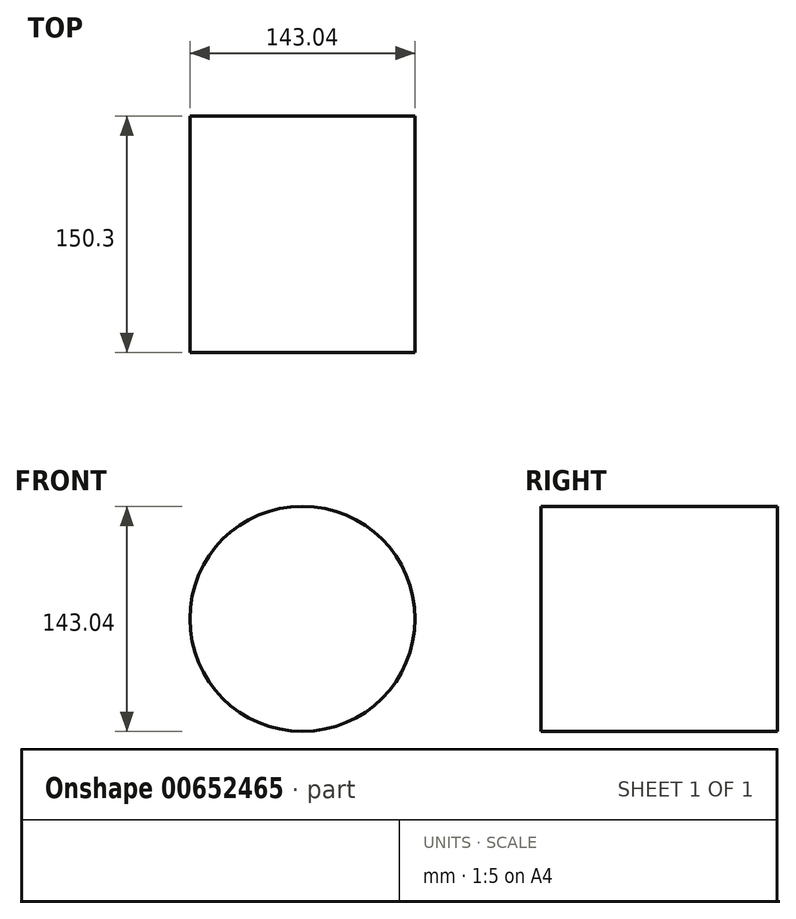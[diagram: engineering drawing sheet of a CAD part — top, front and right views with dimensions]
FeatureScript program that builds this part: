
annotation { "Feature Type Name" : "Feature", "Feature Type Description" : "" }
export const myFeature = defineFeature(function(context is Context, id is Id, definition is map)
    precondition{}
    {
        {
            var Q0;
            Q0=qCreatedBy(makeId("Front.planeOp"),FACE);
            var sketch = newSketch(context, id + "F0", { "sketchPlane" : qUnion([Q0])});
            skCircle(sketch, "E0", {"center": v(0, 0) * mm, "radius": 71.52 * mm});
            skSolve(sketch);
        }
        {
            var Q0;
            Q0=makeQuery(id+"F0.imprint","IMPRINT",FACE,{"disambiguationData":[TD([[makeQuery(id+"F0.imprint","IMPRINT",EDGE,{"derivedFrom":sQuery(id+"F0.wireOp",EDGE,"E0")}),1.0]])]});
            extrude(context, id + "F1", {"entities" : qUnion([Q0]), "depth" : 150.3 * mm, "offsetDistance" : 25.4 * mm});
        }
    });
